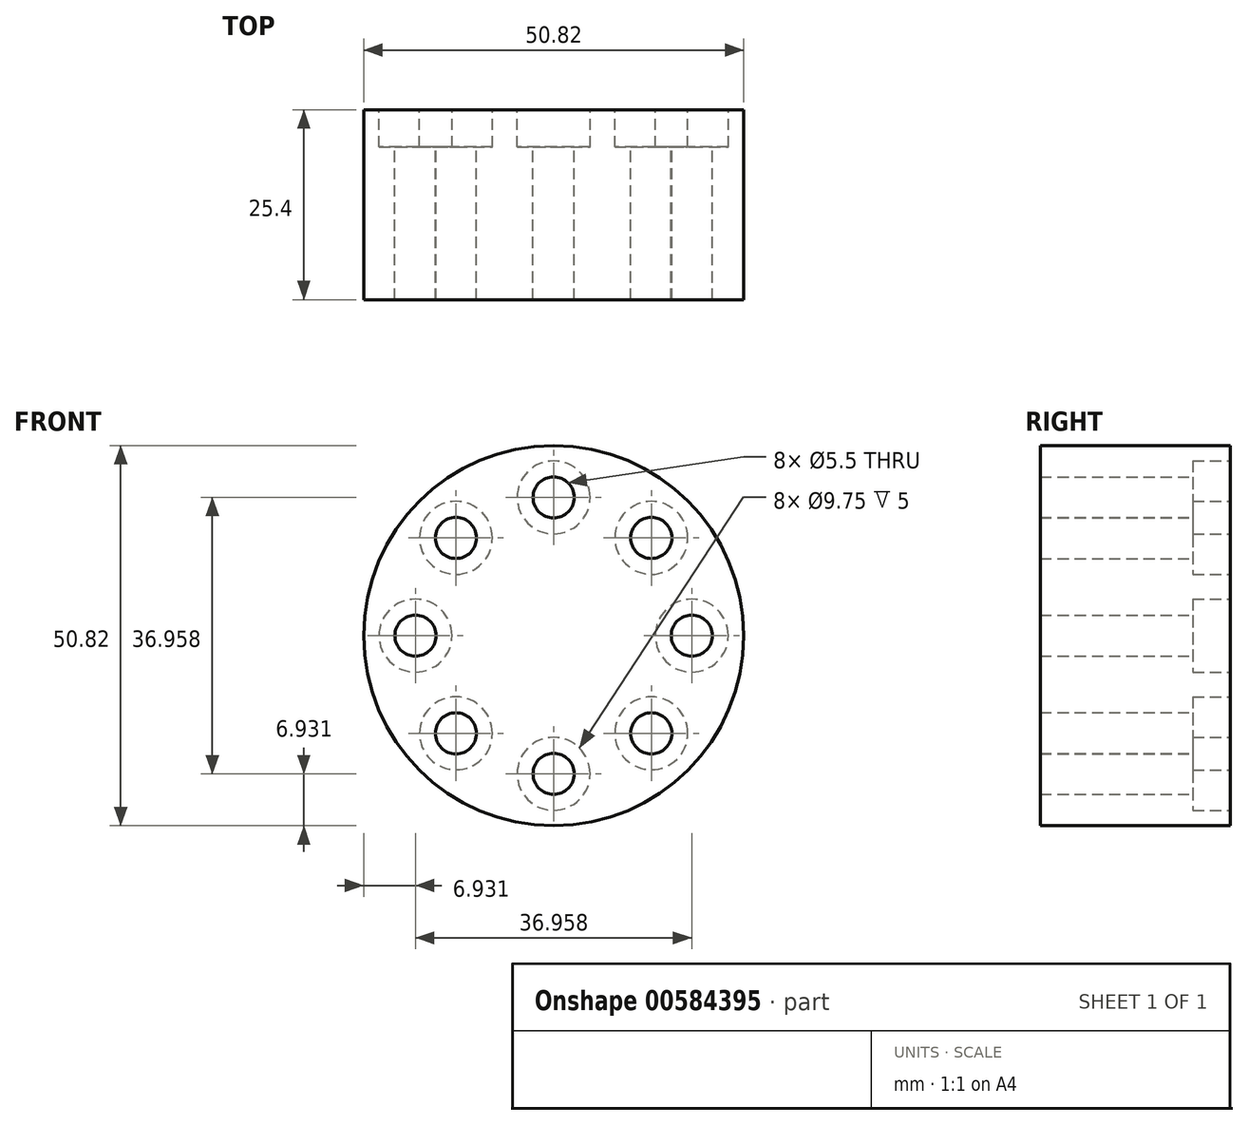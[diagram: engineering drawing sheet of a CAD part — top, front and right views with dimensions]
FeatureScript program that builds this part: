
annotation { "Feature Type Name" : "Feature", "Feature Type Description" : "" }
export const myFeature = defineFeature(function(context is Context, id is Id, definition is map)
    precondition{}
    {
        {
            var Q0;
            Q0=qCreatedBy(makeId("Front.planeOp"),FACE);
            var sketch = newSketch(context, id + "F0", { "sketchPlane" : qUnion([Q0])});
            skCircle(sketch, "E0", {"center": v(0, 0) * mm, "radius": 25.4 * mm});
            skPoint(sketch, "E1", {"position": v(0, 18.48) * mm});
            skPoint(sketch, "E2.1.0", {"position": v(-13.07, 13.07) * mm});
            skPoint(sketch, "E2.2.0", {"position": v(-18.48, 0) * mm});
            skPoint(sketch, "E2.3.0", {"position": v(-13.07, -13.07) * mm});
            skPoint(sketch, "E2.4.0", {"position": v(0, -18.48) * mm});
            skPoint(sketch, "E2.5.0", {"position": v(13.07, -13.07) * mm});
            skPoint(sketch, "E2.6.0", {"position": v(18.48, 0) * mm});
            skPoint(sketch, "E2.7.0", {"position": v(13.07, 13.07) * mm});
            skSolve(sketch);
        }
        {
            var Q0;
            Q0=makeQuery(id+"F0.imprint","IMPRINT",FACE,{"disambiguationData":[TD([[makeQuery(id+"F0.imprint","IMPRINT",EDGE,{"derivedFrom":sQuery(id+"F0.wireOp",EDGE,"E0")}),1.0]])]});
            extrude(context, id + "F1", {"entities" : qUnion([Q0]), "depth" : 25.4 * mm, "offsetDistance" : 25.4 * mm});
        }
        {
            var Q0;
            Q0=sQuery(id+"F0.wireOp",VERTEX,"E1");
            var Q1;
            Q1=sQuery(id+"F0.wireOp",VERTEX,"E2.1.0");
            var Q2;
            Q2=sQuery(id+"F0.wireOp",VERTEX,"E2.2.0");
            var Q3;
            Q3=sQuery(id+"F0.wireOp",VERTEX,"E2.3.0");
            var Q4;
            Q4=sQuery(id+"F0.wireOp",VERTEX,"E2.4.0");
            var Q5;
            Q5=sQuery(id+"F0.wireOp",VERTEX,"E2.5.0");
            var Q6;
            Q6=sQuery(id+"F0.wireOp",VERTEX,"E2.6.0");
            var Q7;
            Q7=sQuery(id+"F0.wireOp",VERTEX,"E2.7.0");
            var Q8;
            Q8=makeQuery(id+"F1.opExtrude","SWEPT_BODY",BODY,{"disambiguationData":[OSD([sQuery(id+"F0.wireOp",EDGE,"E0")])]});
            hole(context, id + "F2", {"style" : HoleStyle.C_BORE, "endStyle" : HoleEndStyle.THROUGH, "oppositeDirection" : true, "standardTappedOrClearance" : lookupTablePath({ "standard" : "ISO", "fit" : "Normal", "size" : "M5", "type" : "Clearance" }), "standardBlindInLast" : lookupTablePath({ "fit" : "Standard", "standard" : "ISO", "size" : "M5", "type" : "Clearance" }), "holeDiameter" : 5.5 * mm, "cBoreDiameter" : 9.75 * mm, "cBoreDepth" : 5 * mm, "majorDiameter" : 6.35 * mm, "isTappedThrough" : true, "tappedDepth" : 12.7 * mm, "tapClearance" : 3, "startFromSketch" : true, "locations" : qUnion([Q0, Q1, Q2, Q3, Q4, Q5, Q6, Q7]), "scope" : qUnion([Q8])});
        }
    });
